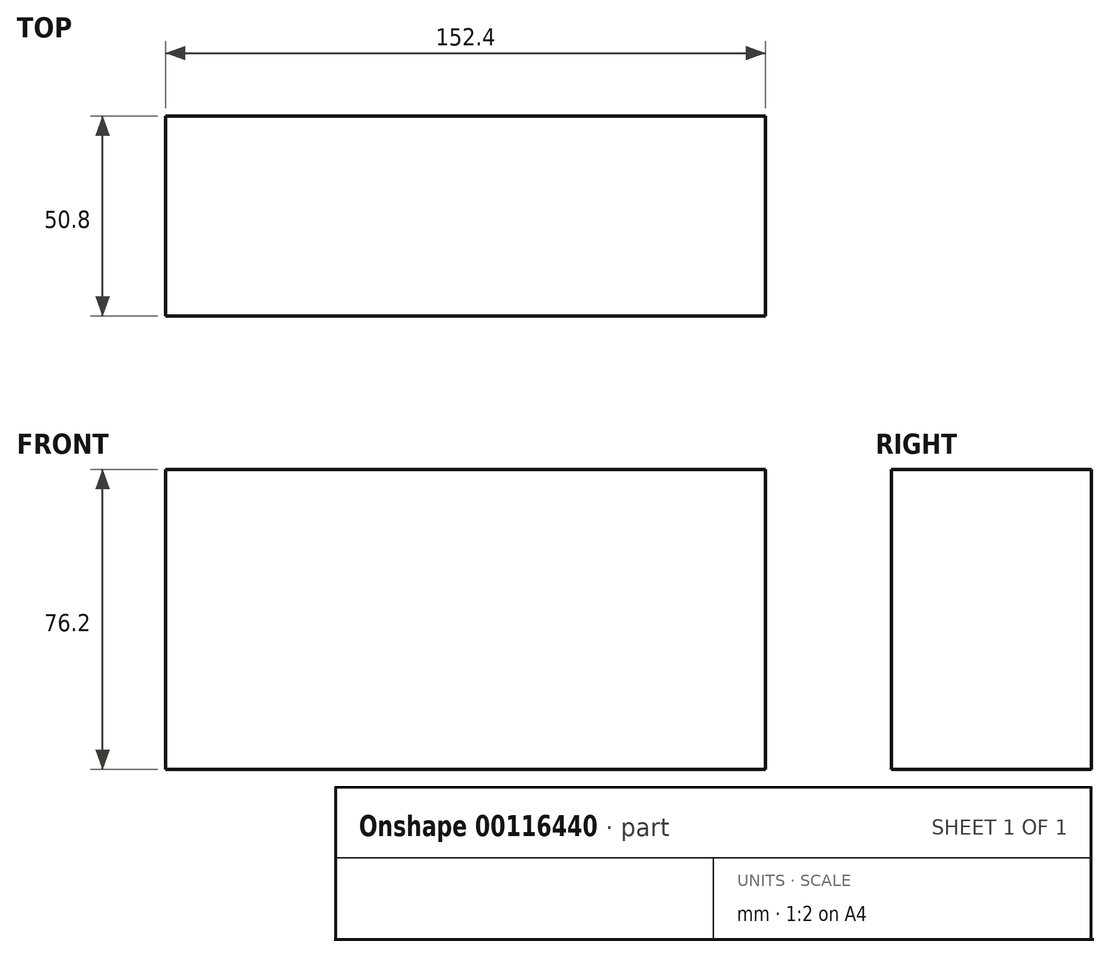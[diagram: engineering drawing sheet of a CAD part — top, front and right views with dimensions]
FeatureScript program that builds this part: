
annotation { "Feature Type Name" : "Feature", "Feature Type Description" : "" }
export const myFeature = defineFeature(function(context is Context, id is Id, definition is map)
    precondition{}
    {
        {
            var Q0;
            Q0=qCreatedBy(makeId("Top.planeOp"),FACE);
            var sketch = newSketch(context, id + "F0", { "sketchPlane" : qUnion([Q0])});
            skLineSegment(sketch, "E0", {"start": v(0, 0) * mm, "end": v(-152.4, 0) * mm});
            skLineSegment(sketch, "E1", {"start": v(-152.4, 0) * mm, "end": v(-152.4, 50.8) * mm});
            skLineSegment(sketch, "E2", {"start": v(-152.4, 50.8) * mm, "end": v(0, 50.8) * mm});
            skLineSegment(sketch, "E3", {"start": v(0, 50.8) * mm, "end": v(0, 0) * mm});
            skSolve(sketch);
        }
        {
            var Q0;
            Q0 = qSketchRegion(id + "F0", true);
            extrude(context, id + "F1", {"entities" : qUnion([Q0]), "depth" : 76.2 * mm});
        }
    });
